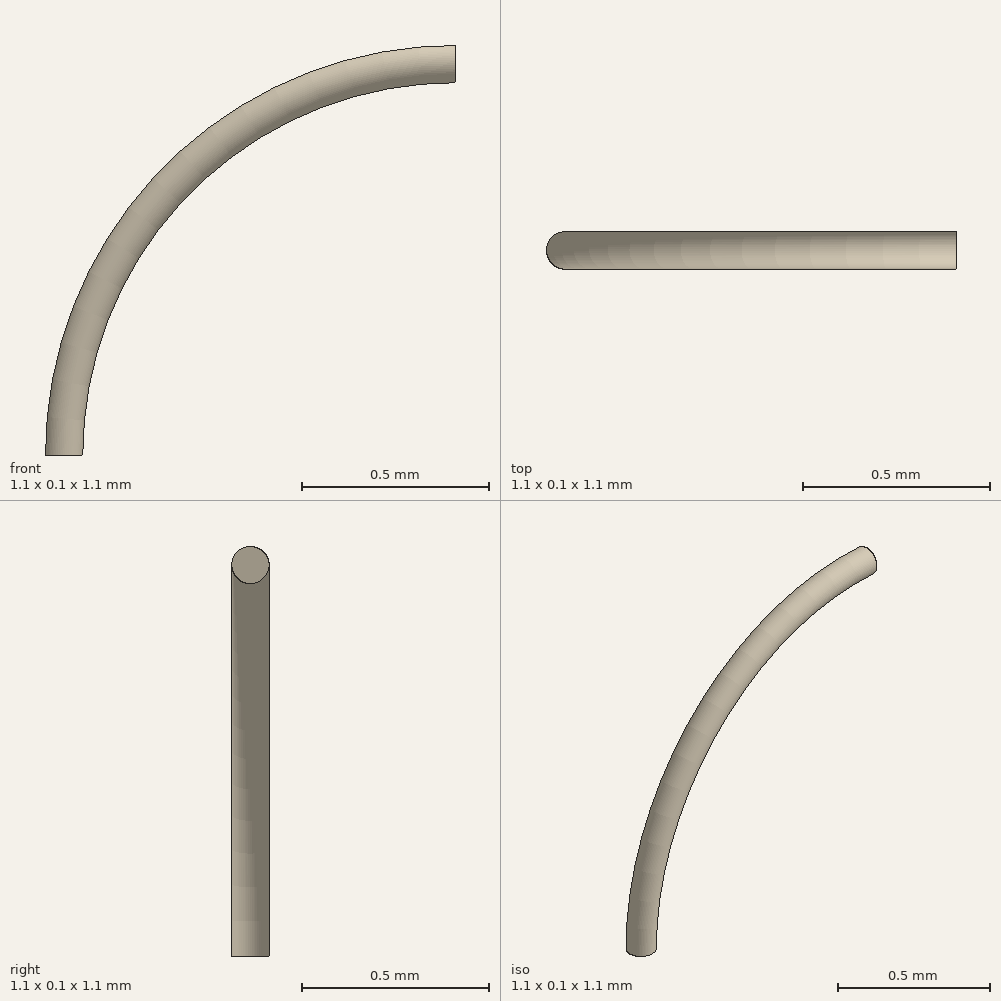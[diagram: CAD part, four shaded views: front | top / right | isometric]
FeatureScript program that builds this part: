
annotation { "Feature Type Name" : "Feature", "Feature Type Description" : "" }
export const myFeature = defineFeature(function(context is Context, id is Id, definition is map)
    precondition{}
    {
        {
            var Q0;
            Q0=qCreatedBy(makeId("Top.planeOp"),FACE);
            var sketch = newSketch(context, id + "F0", { "sketchPlane" : qUnion([Q0])});
            skCircle(sketch, "E0", {"center": v(0, 0) * mm, "radius": 0.05 * mm});
            skSolve(sketch);
        }
        {
            var Q0;
            Q0=qCreatedBy(makeId("Front.planeOp"),FACE);
            var sketch = newSketch(context, id + "F1", { "sketchPlane" : qUnion([Q0])});
            skLineSegment(sketch, "E1.0", {"start": v(-0.05, 0) * mm, "end": v(0.05, 0) * mm});
            skLineSegment(sketch, "E2", {"start": v(0.05, 0) * mm, "end": v(1.05, 0) * mm});
            skLineSegment(sketch, "E3", {"start": v(1.05, 0) * mm, "end": v(1.05, 1) * mm});
            skLineSegment(sketch, "E4", {"start": v(1.05, 1) * mm, "end": v(1.05, 1.1) * mm});
            skPoint(sketch, "E5", {"position": v(1.05, 1.05) * mm});
            skLineSegment(sketch, "E6", {"start": v(1.05, 1.05) * mm, "end": v(1.6, 1.05) * mm});
            skArc(sketch, "E7", {"start": v(1.05, 1.05) * mm, "mid": v(0.3, 0.74) * mm, "end": v(0, 0) * mm});
            skSolve(sketch);
        }
        {
            var Q0;
            Q0=makeQuery(id+"F0.imprint","IMPRINT",FACE,{"disambiguationData":[TD([[makeQuery(id+"F0.imprint","IMPRINT",EDGE,{"derivedFrom":sQuery(id+"F0.wireOp",EDGE,"E0")}),1.0]])]});
            var Q1;
            Q1=sQuery(id+"F1.wireOp",EDGE,"E7");
            sweep(context, id + "F2", {"profiles" : qUnion([Q0]), "path" : qUnion([Q1])});
        }
    });
